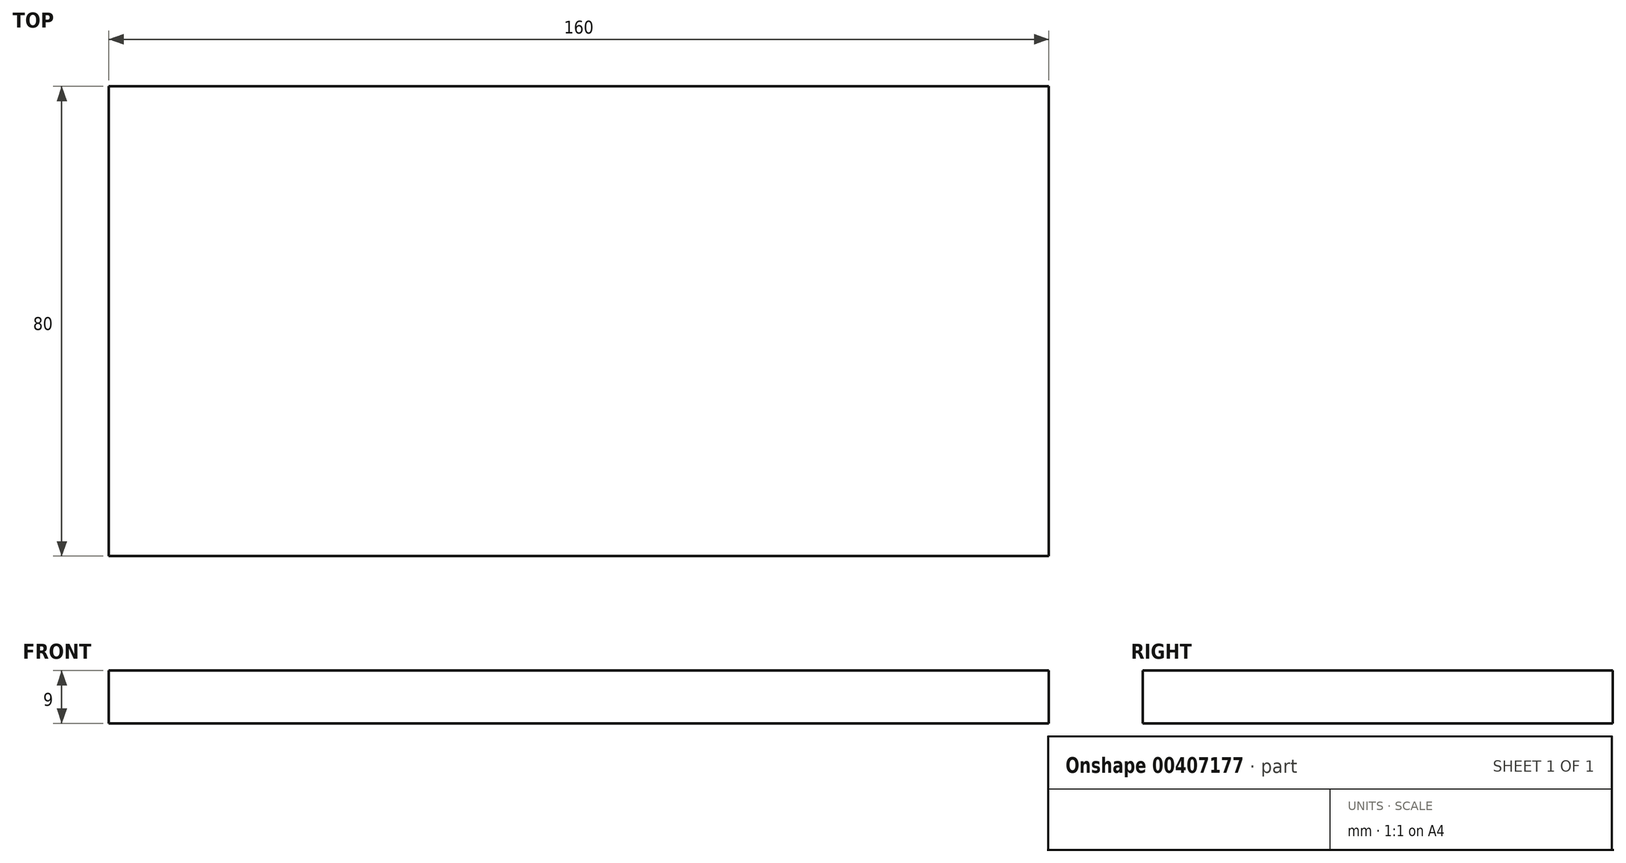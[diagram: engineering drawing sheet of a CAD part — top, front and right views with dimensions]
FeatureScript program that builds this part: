
annotation { "Feature Type Name" : "Feature", "Feature Type Description" : "" }
export const myFeature = defineFeature(function(context is Context, id is Id, definition is map)
    precondition{}
    {
        {
            var Q0;
            Q0=qCreatedBy(makeId("Top.planeOp"),FACE);
            var sketch = newSketch(context, id + "F0", { "sketchPlane" : qUnion([Q0])});
            skLineSegment(sketch, "E0.bottom", {"start": v(80, 40) * mm, "end": v(-80, 40) * mm});
            skLineSegment(sketch, "E0.top", {"start": v(80, -40) * mm, "end": v(-80, -40) * mm});
            skLineSegment(sketch, "E0.left", {"start": v(80, 40) * mm, "end": v(80, -40) * mm});
            skLineSegment(sketch, "E0.right", {"start": v(-80, 40) * mm, "end": v(-80, -40) * mm});
            skPoint(sketch, "E0.middle", {"position": v(0, 0) * mm});
            skSolve(sketch);
        }
        {
            var Q0;
            Q0 = qSketchRegion(id + "F0", true);
            extrude(context, id + "F1", {"entities" : qUnion([Q0]), "depth" : 9 * mm});
        }
    });
